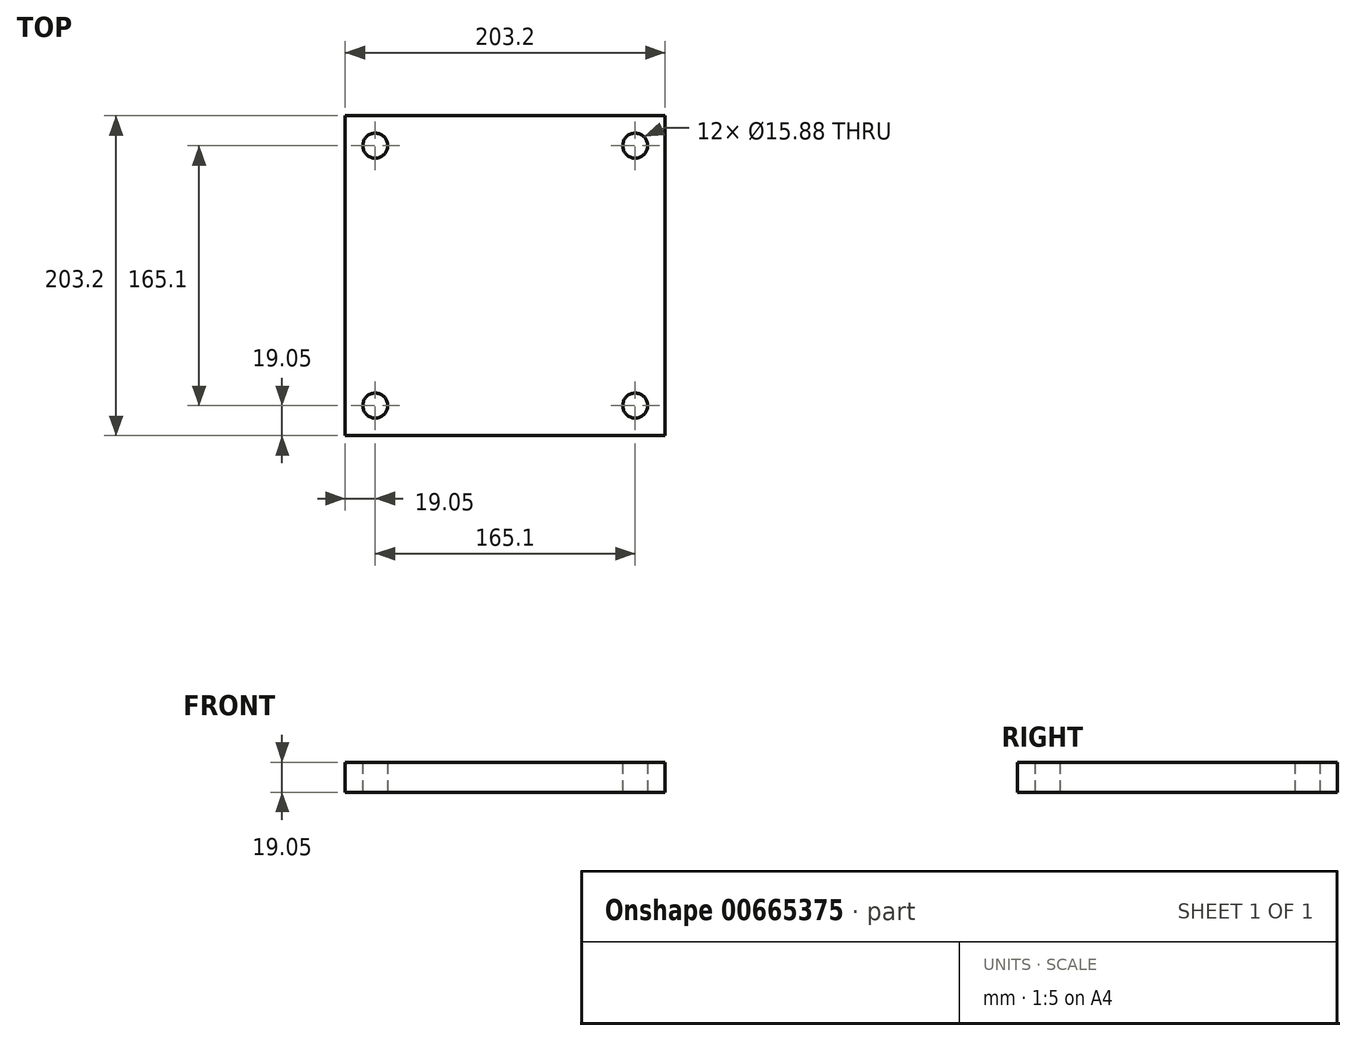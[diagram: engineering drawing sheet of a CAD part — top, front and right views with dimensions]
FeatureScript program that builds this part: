
annotation { "Feature Type Name" : "Feature", "Feature Type Description" : "" }
export const myFeature = defineFeature(function(context is Context, id is Id, definition is map)
    precondition{}
    {
        {
            var Q0;
            Q0=qCreatedBy(makeId("Top.planeOp"),FACE);
            var sketch = newSketch(context, id + "F0", { "sketchPlane" : qUnion([Q0])});
            skLineSegment(sketch, "E0.bottom", {"start": v(-101.6, -101.6) * mm, "end": v(101.6, -101.6) * mm});
            skLineSegment(sketch, "E0.top", {"start": v(-101.6, 101.6) * mm, "end": v(101.6, 101.6) * mm});
            skLineSegment(sketch, "E0.left", {"start": v(-101.6, -101.6) * mm, "end": v(-101.6, 101.6) * mm});
            skLineSegment(sketch, "E0.right", {"start": v(101.6, -101.6) * mm, "end": v(101.6, 101.6) * mm});
            skPoint(sketch, "E0.middle", {"position": v(0, 0) * mm});
            skCircle(sketch, "E1", {"center": v(-82.55, 82.55) * mm, "radius": 7.94 * mm});
            skCircle(sketch, "E2", {"center": v(82.55, -82.55) * mm, "radius": 7.94 * mm});
            skCircle(sketch, "E3", {"center": v(82.55, 82.55) * mm, "radius": 7.94 * mm});
            skCircle(sketch, "E4", {"center": v(-82.55, -82.55) * mm, "radius": 7.94 * mm});
            skLineSegment(sketch, "E5.bottom", {"start": v(-82.55, 82.55) * mm, "end": v(82.55, 82.55) * mm, "construction": true});
            skLineSegment(sketch, "E5.top", {"start": v(-82.55, -82.55) * mm, "end": v(82.55, -82.55) * mm, "construction": true});
            skLineSegment(sketch, "E5.left", {"start": v(-82.55, 82.55) * mm, "end": v(-82.55, -82.55) * mm, "construction": true});
            skLineSegment(sketch, "E5.right", {"start": v(82.55, 82.55) * mm, "end": v(82.55, -82.55) * mm, "construction": true});
            skSolve(sketch);
        }
        {
            var Q0;
            Q0 = qSketchRegion(id + "F0", true);
            extrude(context, id + "F1", {"entities" : qUnion([Q0]), "depth" : 19.05 * mm, "offsetDistance" : 25.4 * mm});
        }
    });
